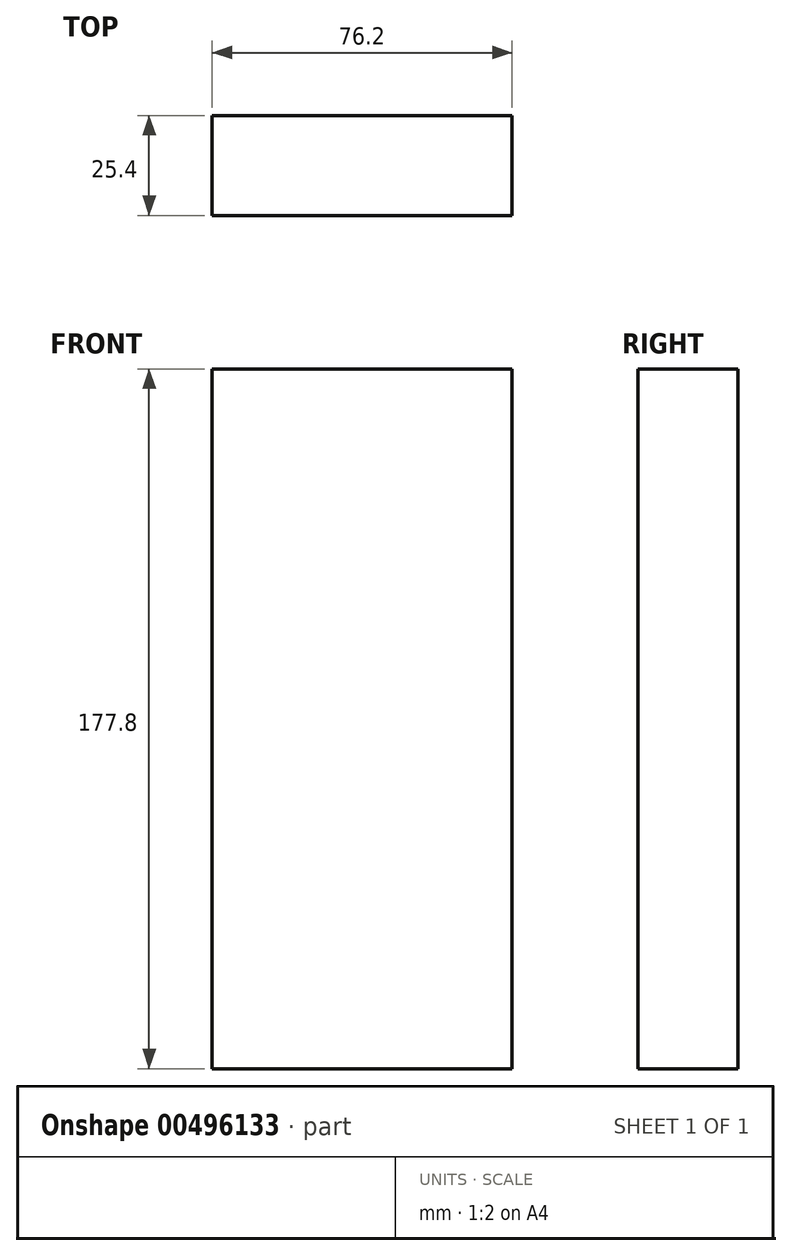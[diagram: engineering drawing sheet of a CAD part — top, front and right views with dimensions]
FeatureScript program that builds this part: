
annotation { "Feature Type Name" : "Feature", "Feature Type Description" : "" }
export const myFeature = defineFeature(function(context is Context, id is Id, definition is map)
    precondition{}
    {
        {
            var Q0;
            Q0=qCreatedBy(makeId("Front.planeOp"),FACE);
            var sketch = newSketch(context, id + "F0", { "sketchPlane" : qUnion([Q0])});
            skLineSegment(sketch, "E0", {"start": v(-28.01, 93.38) * mm, "end": v(-28.01, -84.42) * mm});
            skLineSegment(sketch, "E1", {"start": v(-28.01, -84.42) * mm, "end": v(48.19, -84.42) * mm});
            skLineSegment(sketch, "E2", {"start": v(48.19, -84.42) * mm, "end": v(48.19, 93.38) * mm});
            skLineSegment(sketch, "E3", {"start": v(48.19, 93.38) * mm, "end": v(-28.01, 93.38) * mm});
            skSolve(sketch);
        }
        {
            var Q0;
            Q0=makeQuery(id+"F0.imprint","IMPRINT",FACE,{"disambiguationData":[TD([[makeQuery(id+"F0.imprint","IMPRINT",EDGE,{"derivedFrom":sQuery(id+"F0.wireOp",EDGE,"E0")}),1.0]])]});
            extrude(context, id + "F1", {"entities" : qUnion([Q0]), "depth" : 25.4 * mm});
        }
    });
